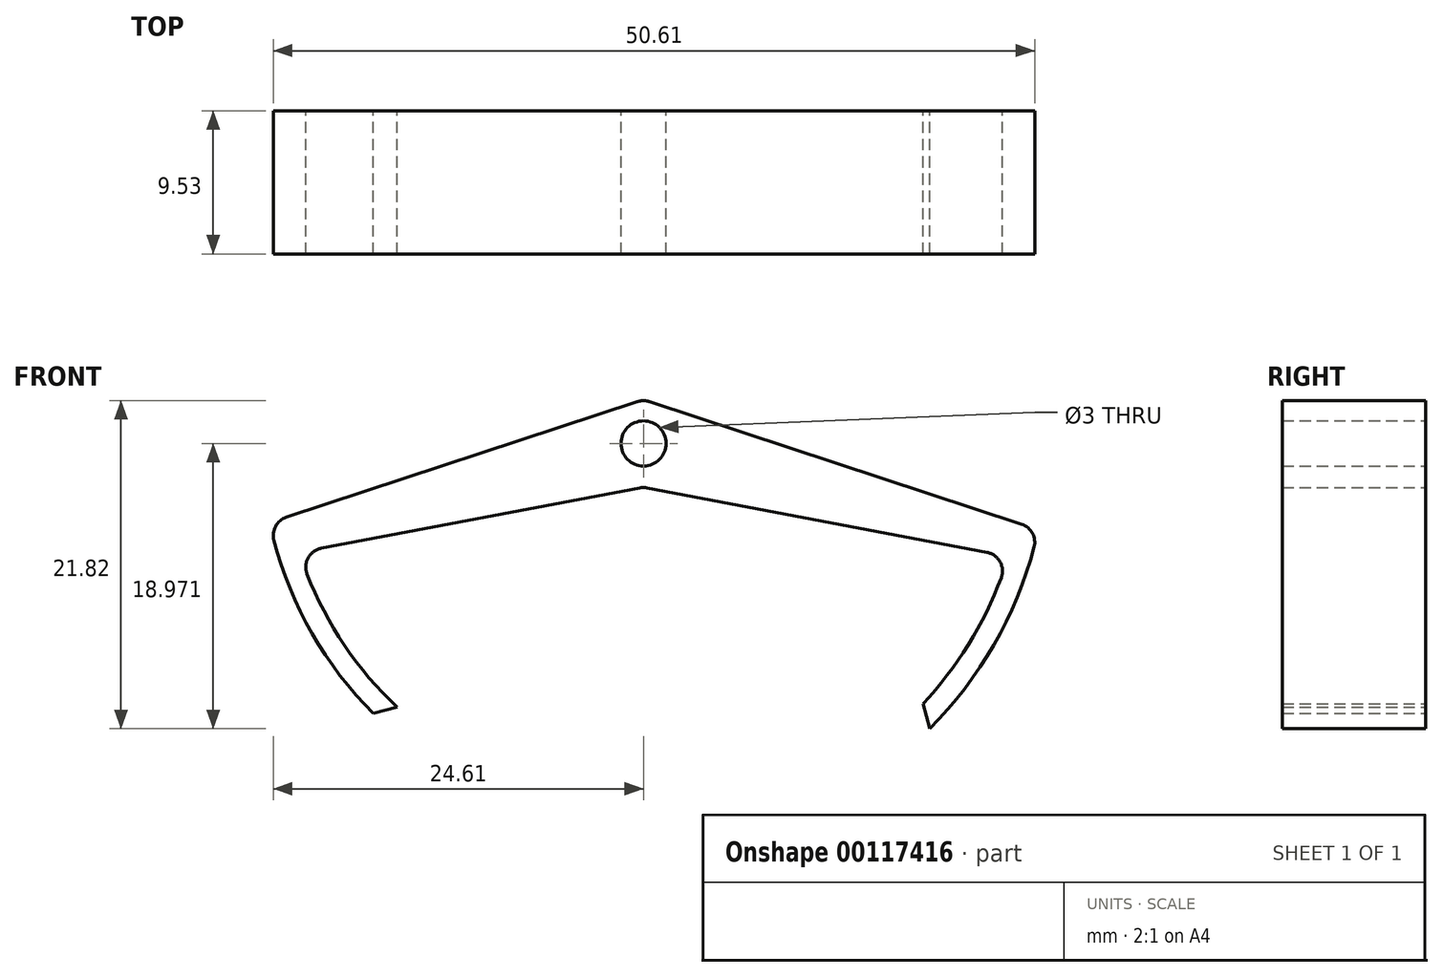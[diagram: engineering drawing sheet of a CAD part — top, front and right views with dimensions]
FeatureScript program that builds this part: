
annotation { "Feature Type Name" : "Feature", "Feature Type Description" : "" }
export const myFeature = defineFeature(function(context is Context, id is Id, definition is map)
    precondition{}
    {
        {
            var Q0;
            Q0=qCreatedBy(makeId("Front.planeOp"),FACE);
            var sketch = newSketch(context, id + "F0", { "sketchPlane" : qUnion([Q0])});
            skArc(sketch, "E0", {"start": v(-24.57, 14.8) * mm, "mid": v(-22.03, 8.6) * mm, "end": v(-17.96, 3.27) * mm});
            skLineSegment(sketch, "E1", {"start": v(-17.96, 3.27) * mm, "end": v(-16.37, 3.7) * mm});
            skLineSegment(sketch, "E2", {"start": v(18.58, 3.9) * mm, "end": v(19.02, 2.26) * mm});
            skArc(sketch, "E3", {"start": v(19.02, 2.26) * mm, "mid": v(23.28, 7.84) * mm, "end": v(25.96, 14.33) * mm});
            skLineSegment(sketch, "E4", {"start": v(-0.24, 18.28) * mm, "end": v(-21.42, 14.25) * mm});
            skLineSegment(sketch, "E5", {"start": v(-0.4, 24.01) * mm, "end": v(-23.74, 16.32) * mm});
            skLineSegment(sketch, "E6.MirrorCS", {"start": v(0.4, 24.01) * mm, "end": v(25.13, 15.86) * mm});
            skLineSegment(sketch, "E7.MirrorCS", {"start": v(0.24, 18.28) * mm, "end": v(22.82, 13.99) * mm});
            skPoint(sketch, "E8.orphan", {"position": v(-32.7, 12.11) * mm});
            skPoint(sketch, "E9.orphan", {"position": v(-40.06, 10.94) * mm});
            skPoint(sketch, "E10.orphan", {"position": v(32.7, 12.11) * mm});
            skPoint(sketch, "E11.orphan", {"position": v(40.06, 10.94) * mm});
            skArc(sketch, "E12.trimOffspring", {"start": v(-22.36, 12.55) * mm, "mid": v(-19.87, 7.78) * mm, "end": v(-16.37, 3.7) * mm});
            skArc(sketch, "E13.trimOffspring", {"start": v(18.58, 3.9) * mm, "mid": v(21.59, 7.85) * mm, "end": v(23.78, 12.3) * mm});
            skCircle(sketch, "E14", {"center": v(0, 21.23) * mm, "radius": 1.5 * mm});
            skPoint(sketch, "E15.visualSharp", {"position": v(-24.85, 15.95) * mm});
            skArc(sketch, "E15.filletArc", {"start": v(-23.74, 16.32) * mm, "mid": v(-24.46, 15.72) * mm, "end": v(-24.57, 14.8) * mm});
            skPoint(sketch, "E16.visualSharp", {"position": v(26.24, 15.5) * mm});
            skArc(sketch, "E16.filletArc", {"start": v(25.96, 14.33) * mm, "mid": v(25.85, 15.26) * mm, "end": v(25.13, 15.86) * mm});
            skPoint(sketch, "E17.visualSharp", {"position": v(24.26, 13.71) * mm});
            skArc(sketch, "E17.filletArc", {"start": v(23.78, 12.3) * mm, "mid": v(23.7, 13.36) * mm, "end": v(22.82, 13.99) * mm});
            skPoint(sketch, "E18.visualSharp", {"position": v(-22.87, 13.98) * mm});
            skArc(sketch, "E18.filletArc", {"start": v(-21.42, 14.25) * mm, "mid": v(-22.3, 13.62) * mm, "end": v(-22.36, 12.55) * mm});
            skPoint(sketch, "E19.visualSharp", {"position": v(0, 24.14) * mm});
            skArc(sketch, "E19.filletArc", {"start": v(0.4, 24.01) * mm, "mid": v(0, 24.08) * mm, "end": v(-0.4, 24.01) * mm});
            skPoint(sketch, "E20.visualSharp", {"position": v(0, 18.32) * mm});
            skArc(sketch, "E20.filletArc", {"start": v(0.24, 18.28) * mm, "mid": v(0, 18.3) * mm, "end": v(-0.24, 18.28) * mm});
            skSolve(sketch);
        }
        {
            var Q0;
            Q0 = qSketchRegion(id + "F0", true);
            extrude(context, id + "F1", {"entities" : qUnion([Q0]), "depth" : 9.52 * mm});
        }
    });
